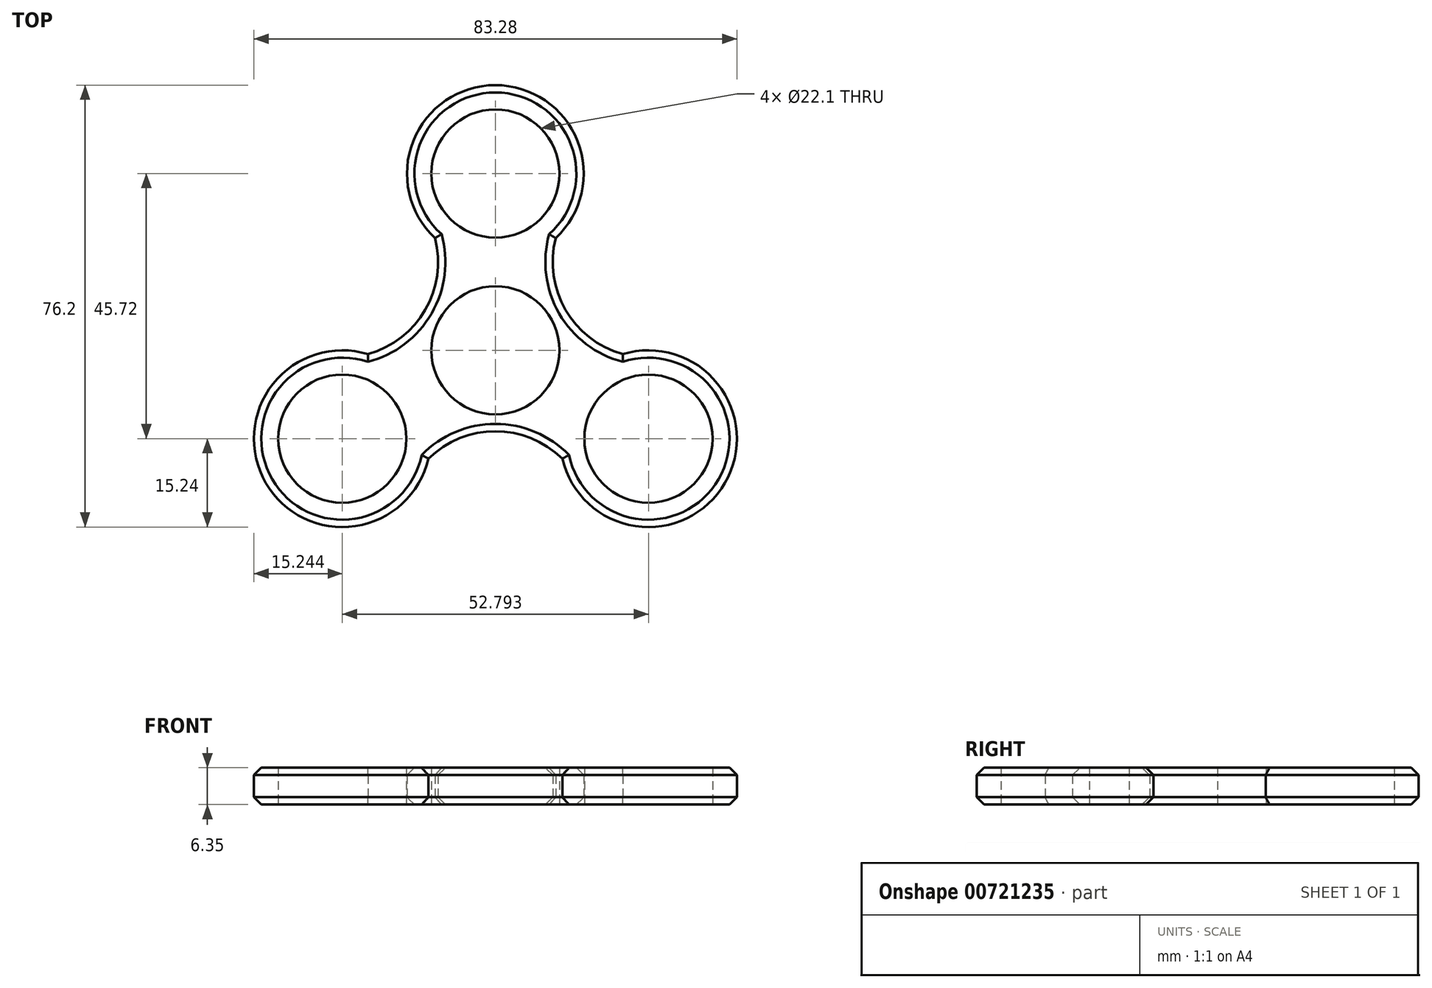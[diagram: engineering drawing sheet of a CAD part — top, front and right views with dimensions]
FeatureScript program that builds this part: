
annotation { "Feature Type Name" : "Feature", "Feature Type Description" : "" }
export const myFeature = defineFeature(function(context is Context, id is Id, definition is map)
    precondition{}
    {
        {
            var Q0;
            Q0=qCreatedBy(makeId("Top.planeOp"),FACE);
            var sketch = newSketch(context, id + "F0", { "sketchPlane" : qUnion([Q0])});
            skCircle(sketch, "E0", {"center": v(0, 0) * mm, "radius": 11.05 * mm});
            skCircle(sketch, "E1", {"center": v(0, 0) * mm, "radius": 13.97 * mm});
            skLineSegment(sketch, "E2", {"start": v(0, 0) * mm, "end": v(0, 30.48) * mm});
            skCircle(sketch, "E3", {"center": v(0, 30.48) * mm, "radius": 11.05 * mm});
            skCircle(sketch, "E4", {"center": v(0, 30.48) * mm, "radius": 15.24 * mm});
            skCircle(sketch, "E5.1.0", {"center": v(-26.4, -15.24) * mm, "radius": 11.05 * mm});
            skCircle(sketch, "E5.2.0", {"center": v(26.4, -15.24) * mm, "radius": 11.05 * mm});
            skCircle(sketch, "E6.1.0", {"center": v(-26.4, -15.24) * mm, "radius": 15.24 * mm});
            skCircle(sketch, "E6.2.0", {"center": v(26.4, -15.24) * mm, "radius": 15.24 * mm});
            skLineSegment(sketch, "E7", {"start": v(0, 0) * mm, "end": v(-26.4, 15.24) * mm});
            skArc(sketch, "E8", {"start": v(-30.84, -0.66) * mm, "mid": v(-12.1, 6.99) * mm, "end": v(-14.85, 27.04) * mm});
            skArc(sketch, "E9.1.0", {"start": v(16, -26.38) * mm, "mid": v(0, -13.97) * mm, "end": v(-16, -26.38) * mm});
            skArc(sketch, "E9.2.0", {"start": v(14.85, 27.04) * mm, "mid": v(12.1, 6.98) * mm, "end": v(30.84, -0.66) * mm});
            skSolve(sketch);
        }
        {
            var Q0;
            Q0 = qSketchRegion(id + "F0", true);
            extrude(context, id + "F1", {"entities" : qUnion([Q0]), "depth" : 6.35 * mm, "offsetDistance" : 25.4 * mm});
        }
        {
            var Q0;
            Q0=makeQuery(id+"F1.opExtrude","CAP_EDGE",EDGE,{"disambiguationData":[OSD([sQuery(id+"F0.wireOp",EDGE,"E4")])],"isStart":false});
            var Q1;
            Q1=makeQuery(id+"F1.opExtrude","CAP_EDGE",EDGE,{"disambiguationData":[OSD([sQuery(id+"F0.wireOp",EDGE,"E8")])],"isStart":false});
            var Q2;
            Q2=makeQuery(id+"F1.opExtrude","CAP_EDGE",EDGE,{"disambiguationData":[OSD([sQuery(id+"F0.wireOp",EDGE,"E9.2.0")])],"isStart":false});
            var Q3;
            Q3=makeQuery(id+"F1.opExtrude","CAP_EDGE",EDGE,{"disambiguationData":[OSD([sQuery(id+"F0.wireOp",EDGE,"E6.2.0")])],"isStart":false});
            var Q4;
            Q4=makeQuery(id+"F1.opExtrude","CAP_EDGE",EDGE,{"disambiguationData":[OSD([sQuery(id+"F0.wireOp",EDGE,"E9.1.0")])],"isStart":false});
            var Q5;
            Q5=makeQuery(id+"F1.opExtrude","CAP_EDGE",EDGE,{"disambiguationData":[OSD([sQuery(id+"F0.wireOp",EDGE,"E6.1.0")])],"isStart":false});
            chamfer(context, id + "F2", {"entities" : qUnion([Q0, Q1, Q2, Q3, Q4, Q5]), "width" : 1.27 * mm, "tangentPropagation" : true});
        }
        {
            var Q0;
            Q0=makeQuery(id+"F1.opExtrude","CAP_EDGE",EDGE,{"disambiguationData":[OSD([sQuery(id+"F0.wireOp",EDGE,"E4")])],"isStart":true});
            var Q1;
            Q1=makeQuery(id+"F1.opExtrude","CAP_EDGE",EDGE,{"disambiguationData":[OSD([sQuery(id+"F0.wireOp",EDGE,"E8")])],"isStart":true});
            var Q2;
            Q2=makeQuery(id+"F1.opExtrude","CAP_EDGE",EDGE,{"disambiguationData":[OSD([sQuery(id+"F0.wireOp",EDGE,"E6.1.0")])],"isStart":true});
            var Q3;
            Q3=makeQuery(id+"F1.opExtrude","CAP_EDGE",EDGE,{"disambiguationData":[OSD([sQuery(id+"F0.wireOp",EDGE,"E9.2.0")])],"isStart":true});
            var Q4;
            Q4=makeQuery(id+"F1.opExtrude","CAP_EDGE",EDGE,{"disambiguationData":[OSD([sQuery(id+"F0.wireOp",EDGE,"E6.2.0")])],"isStart":true});
            var Q5;
            Q5=makeQuery(id+"F1.opExtrude","CAP_EDGE",EDGE,{"disambiguationData":[OSD([sQuery(id+"F0.wireOp",EDGE,"E9.1.0")])],"isStart":true});
            chamfer(context, id + "F3", {"entities" : qUnion([Q0, Q1, Q2, Q3, Q4, Q5]), "width" : 1.27 * mm, "tangentPropagation" : true});
        }
    });
